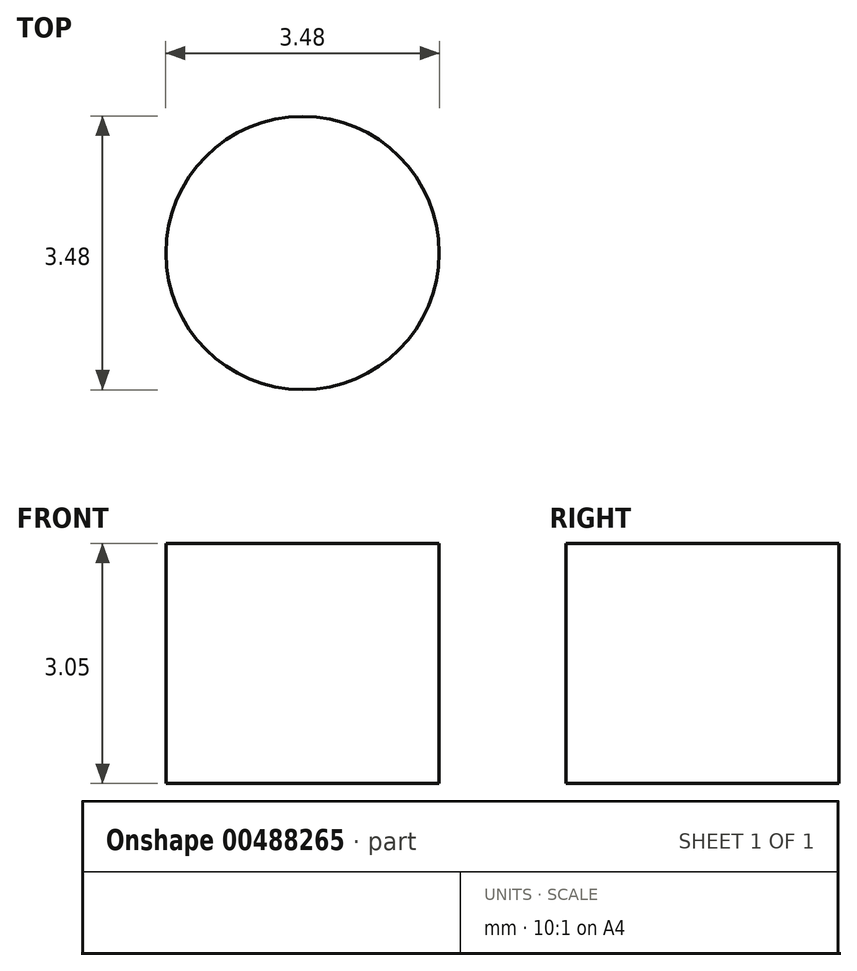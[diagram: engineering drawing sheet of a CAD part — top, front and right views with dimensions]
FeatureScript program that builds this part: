
annotation { "Feature Type Name" : "Feature", "Feature Type Description" : "" }
export const myFeature = defineFeature(function(context is Context, id is Id, definition is map)
    precondition{}
    {
        {
            var Q0;
            Q0=qCreatedBy(makeId("Top.planeOp"),FACE);
            var sketch = newSketch(context, id + "F0", { "sketchPlane" : qUnion([Q0])});
            skCircle(sketch, "E0", {"center": v(0, 0) * mm, "radius": 1.74 * mm});
            skSolve(sketch);
        }
        {
            var Q0;
            Q0=makeQuery(id+"F0.imprint","IMPRINT",FACE,{"disambiguationData":[TD([[makeQuery(id+"F0.imprint","IMPRINT",EDGE,{"derivedFrom":sQuery(id+"F0.wireOp",EDGE,"E0")}),1.0]])]});
            extrude(context, id + "F1", {"entities" : qUnion([Q0]), "depth" : 3.05 * mm});
        }
    });
